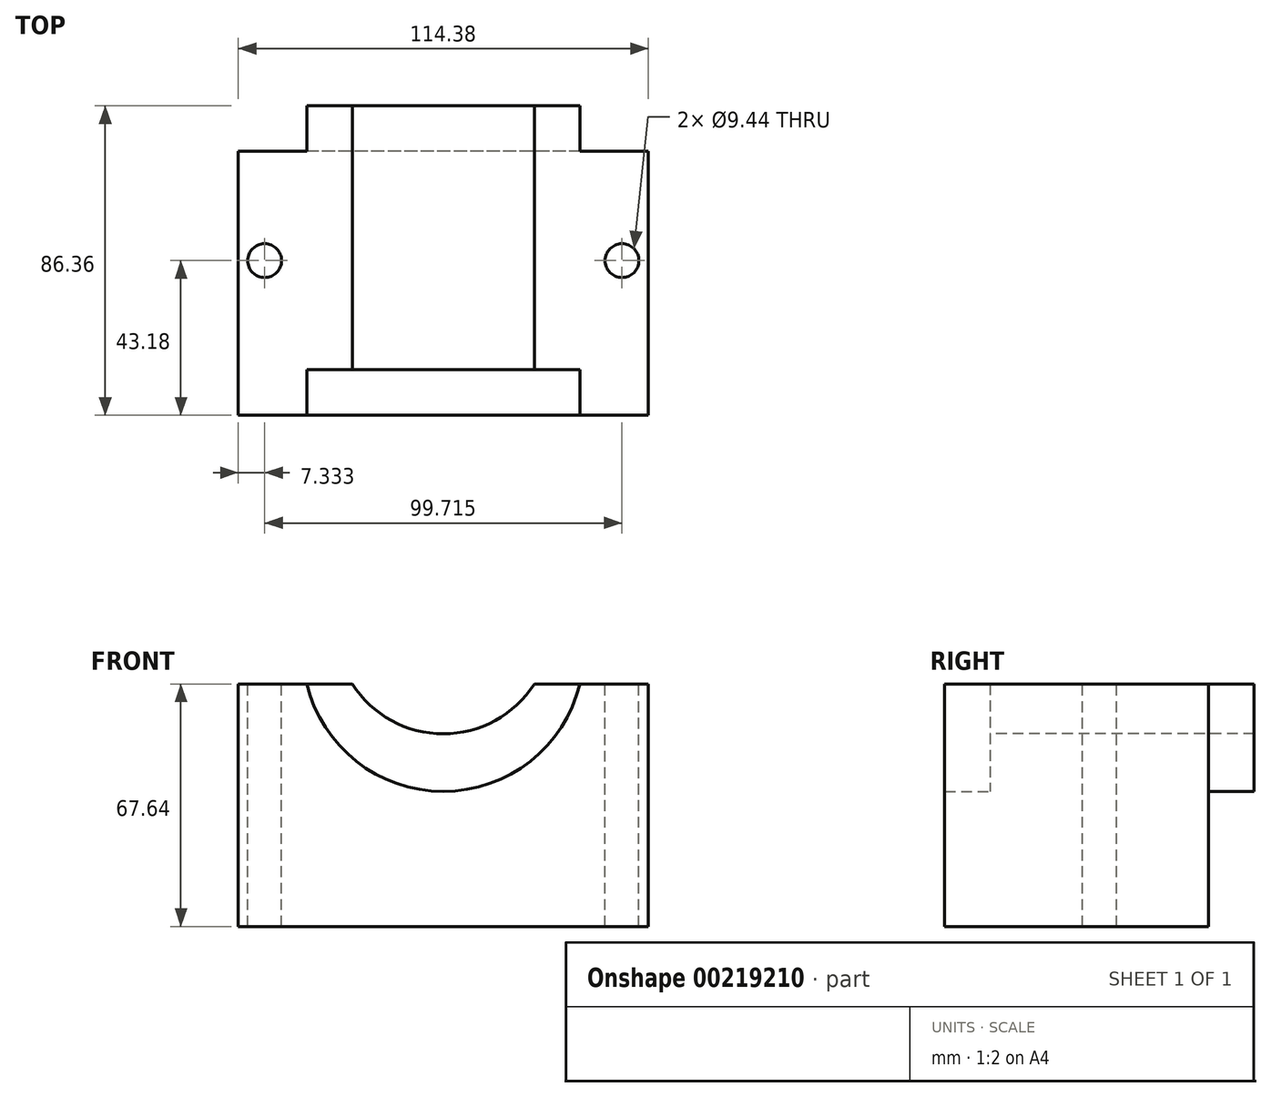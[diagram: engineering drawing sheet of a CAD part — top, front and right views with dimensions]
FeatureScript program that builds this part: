
annotation { "Feature Type Name" : "Feature", "Feature Type Description" : "" }
export const myFeature = defineFeature(function(context is Context, id is Id, definition is map)
    precondition{}
    {
        {
            var Q0;
            Q0=qCreatedBy(makeId("Front.planeOp"),FACE);
            var sketch = newSketch(context, id + "F0", { "sketchPlane" : qUnion([Q0])});
            skLineSegment(sketch, "E0.bottom", {"start": v(57.19, 33.82) * mm, "end": v(-57.19, 33.82) * mm});
            skLineSegment(sketch, "E0.top", {"start": v(57.19, -33.82) * mm, "end": v(-57.19, -33.82) * mm});
            skLineSegment(sketch, "E0.left", {"start": v(57.19, 33.82) * mm, "end": v(57.19, -33.82) * mm});
            skLineSegment(sketch, "E0.right", {"start": v(-57.19, 33.82) * mm, "end": v(-57.19, -33.82) * mm});
            skPoint(sketch, "E0.middle", {"position": v(0, 0) * mm});
            skSolve(sketch);
        }
        {
            var Q0;
            Q0 = qSketchRegion(id + "F0", true);
            extrude(context, id + "F1", {"entities" : qUnion([Q0]), "oppositeDirection" : true, "depth" : 60.96 * mm});
        }
        {
            var Q0;
            Q0=makeQuery(id+"F1.opExtrude","CAP_FACE",FACE,{"disambiguationData":[OSD([sQuery(id+"F0.wireOp",EDGE,"E0.bottom"),sQuery(id+"F0.wireOp",EDGE,"E0.top"),sQuery(id+"F0.wireOp",EDGE,"E0.left"),sQuery(id+"F0.wireOp",EDGE,"E0.right")])],"isStart":false});
            var sketch = newSketch(context, id + "F2", { "sketchPlane" : qUnion([Q0])});
            skLineSegment(sketch, "E1", {"start": v(0, 33.82) * mm, "end": v(0, 59.11) * mm});
            skPoint(sketch, "E1.endSnap0", {"position": v(0, 33.82) * mm});
            skLineSegment(sketch, "E2.0", {"start": v(-38.1, 33.82) * mm, "end": v(-38.1, 59.11) * mm});
            skLineSegment(sketch, "E3.0", {"start": v(38.1, 33.82) * mm, "end": v(38.1, 59.11) * mm});
            skArc(sketch, "E4", {"start": v(-38.1, 33.82) * mm, "mid": v(0, 3.86) * mm, "end": v(38.1, 33.82) * mm});
            skLineSegment(sketch, "E5", {"start": v(-38.1, 33.82) * mm, "end": v(38.1, 33.82) * mm});
            skSolve(sketch);
        }
        {
            var Q0;
            Q0 = qSketchRegion(id + "F2", true);
            extrude(context, id + "F3", {"entities" : qUnion([Q0]), "operationType" : NewBodyOperationType.ADD, "depth" : 12.7 * mm});
        }
        {
            var Q0;
            Q0=makeQuery(id+"F1.opExtrude","CAP_FACE",FACE,{"disambiguationData":[OSD([sQuery(id+"F0.wireOp",EDGE,"E0.bottom"),sQuery(id+"F0.wireOp",EDGE,"E0.top"),sQuery(id+"F0.wireOp",EDGE,"E0.left"),sQuery(id+"F0.wireOp",EDGE,"E0.right")])],"isStart":true});
            var sketch = newSketch(context, id + "F4", { "sketchPlane" : qUnion([Q0])});
            skPoint(sketch, "E6.endSnap0", {"position": v(0, 33.82) * mm});
            skArc(sketch, "E7.0", {"start": v(38.1, 33.82) * mm, "mid": v(0, 3.86) * mm, "end": v(-38.1, 33.82) * mm});
            skSolve(sketch);
        }
        {
            var Q0;
            Q0 = qSketchRegion(id + "F4", true);
            var Q1;
            {var subQ0=sQuery(id+"F4.wireOp",EDGE,"E7.0");Q1=makeQuery(id+"F4.imprint","IMPRINT",FACE,{"disambiguationData":[TD([[makeQuery(id+"F4.imprint","IMPRINT",EDGE,{"derivedFrom":subQ0}),-1.0]])]});}
            extrude(context, id + "F5", {"entities" : qUnion([Q0, Q1]), "operationType" : NewBodyOperationType.ADD, "depth" : 12.7 * mm});
        }
        {
            var Q0;
            Q0=makeQuery(id+"F5.opExtrude","CAP_FACE",FACE,{"disambiguationData":[OSD([sQuery(id+"F0.wireOp",EDGE,"E0.bottom"),sQuery(id+"F4.wireOp",EDGE,"E7.0")])],"isStart":false});
            var sketch = newSketch(context, id + "F6", { "sketchPlane" : qUnion([Q0])});
            skLineSegment(sketch, "E8", {"start": v(0, 33.82) * mm, "end": v(0, 55.08) * mm});
            skLineSegment(sketch, "E9.0", {"start": v(25.4, 33.82) * mm, "end": v(25.4, 55.08) * mm});
            skLineSegment(sketch, "E10.0", {"start": v(-25.4, 33.82) * mm, "end": v(-25.4, 55.08) * mm});
            skArc(sketch, "E11", {"start": v(-25.4, 33.82) * mm, "mid": v(0, 19.96) * mm, "end": v(25.4, 33.82) * mm});
            skLineSegment(sketch, "E12", {"start": v(25.4, 33.82) * mm, "end": v(-25.4, 33.82) * mm});
            skSolve(sketch);
        }
        {
            var Q0;
            Q0 = qSketchRegion(id + "F6", true);
            extrude(context, id + "F7", {"entities" : qUnion([Q0]), "operationType" : NewBodyOperationType.REMOVE, "endBound" : BoundingType.THROUGH_ALL, "oppositeDirection" : true, "depth" : 25.4 * mm});
        }
        {
            var Q0;
            {var subQ0=sQuery(id+"F0.wireOp",EDGE,"E0.right");var subQ4=sQuery(id+"F0.wireOp",EDGE,"E0.bottom");var subQ5=sQuery(id+"F2.wireOp",EDGE,"E5");Q0=makeQuery(id+"F7.boolean.opBoolean","SPLIT",FACE,{"disambiguationData":[TD([makeQuery(id+"F1.opExtrude","SWEPT_FACE",FACE,{"disambiguationData":[OSD([subQ0])]})])],"derivedFrom":makeQuery(id+"F5.boolean.opBoolean","MERGE",FACE,{"derivedFrom":[makeQuery(id+"F3.boolean.opBoolean","MERGE",FACE,{"derivedFrom":[makeQuery(id+"F1.opExtrude","SWEPT_FACE",FACE,{"disambiguationData":[OSD([subQ4])]}),makeQuery(id+"F3.opExtrude","SWEPT_FACE",FACE,{"disambiguationData":[OSD([subQ5])]})]}),makeQuery(id+"F5.opExtrude","SWEPT_FACE",FACE,{"disambiguationData":[OSD([subQ4])]})]})});}
            var sketch = newSketch(context, id + "F8", { "sketchPlane" : qUnion([Q0])});
            skCircle(sketch, "E13", {"center": v(-49.86, 30.48) * mm, "radius": 4.72 * mm});
            skPoint(sketch, "E13.centerSnap0", {"position": v(-57.19, 30.48) * mm});
            skCircle(sketch, "E14.MirrorC", {"center": v(49.86, 30.48) * mm, "radius": 4.72 * mm});
            skSolve(sketch);
        }
        {
            var Q0;
            Q0 = qSketchRegion(id + "F8", true);
            extrude(context, id + "F9", {"entities" : qUnion([Q0]), "operationType" : NewBodyOperationType.REMOVE, "endBound" : BoundingType.THROUGH_ALL, "oppositeDirection" : true, "depth" : 25.4 * mm});
        }
    });
